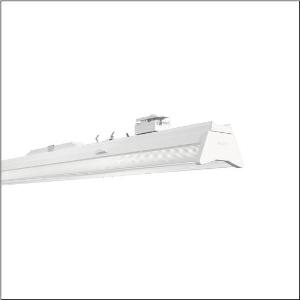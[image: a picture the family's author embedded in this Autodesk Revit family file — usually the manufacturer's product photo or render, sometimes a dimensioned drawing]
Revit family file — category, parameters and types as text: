
# Revit family: licross_21_performance_mo_52td16mn4a5g
name_source: partatom
category: Lighting Fixtures
units: mm (PartAtom-declared; Revit-internal decimal feet)

## family parameters
Cut with Voids When Loaded = No
Host = Face
Light Source = No
Part Type = Normal
Room Calculation Point = No
Round Connector Dimension = Use Diameter
Shared = No

## types (1)
- --- (1 x LED, 10890 lm, 60.5 W, 4000K)
    Apparent Load = 61 VA
    CIE Flux Codes = 66 88 96 79 100
    Color Rendering = 80
    Color Temperature = 4000K
    Default Elevation = 1800 mm
    Description = Licross 21 Performance MO, luminaire insert, of sheet steel, galvanised, coil coated, white, length: 1.500mm, width: 120mm, height: 123mm, LED rated luminous flux: 10.890lm, light colour: 840, SDCM (Standard Deviation of Colour Matching)MacAdam ≤ 3 SDCM (initial), control gear: ON/OFF Multilumen, with plug, 3-pole, with phase selection, mains connection: 220..240V, AC, 50/60Hz, rated input power: 61W, internal wiring halogen-free, primary light control with lens, of plastic, primary optical cover: cover, of PMMA, light emission: direct/indirect distribution, primary light characteristic: symmetric, protection rating (complete): IP54, insulation class (complete): insulation class I (protective earthing), certification: CE, ENEC, UKCA, protection symbol: D if used in an environment with non-conductive dust loads with corresponding accessories, impact resistance: IK06, permissible ambient temperature for indoor applications: -35..+45°C, corresponds to IFS (International Featured Standards) requirements for safety and quality in the food industry, reducing of maximum allowable ambient temperature of 5°C with ceiling mounting, LABS conformity tested according to VDMA 24364:2018-05, The light source and the operating device comply with the requirements of the Ecodesign Regulation (EU) 2019/2020 and are replaceable in accordance with this regulation, packaging unit: 1 piece
    Height = 114 mm
    Lamp = 1 x LED
    Lamp Light Flux = 10890 lm
    Lamp Power = 60.5 W
    Lamp count = 1
    Length = 1500 mm
    Luminous efficacy = 180 lm/W
    Manufacturer = Siteco
    ModVariant = No
    Model = 52TD16MN4A5G
    Mounting Place = Ceiling
    Mounting Type = Pendant
    Number of Poles = 1
    OnlyDefault = Yes
    Power Factor = 1
    Product Name = Licross 21 Performance MO
    Product group = luminaire insert | ceiling pendant
    ProductGroupID = 901
    Protection Class = Protection class I
    Protection Degree = IP 54
    RLX_Detail_Level = 1
    RLX_Emergency_Light_Flux = 0 lm
    RLX_Emergency_Type = 0
    RLX_Emergency_Type_DB = No
    RlxData = <blob elided: 32089 chars, md5=6a0488f3>
    Socket = socket
    Standby Power = 0 W
    System Light Flux = 10890 lm
    System Power = 61 W
    Type Comments = factory setting: luminous flux: 100 % | (A | C | E) | 140 mA
    Type Image = l_1256138.jpg
    URL = http://relux.com
    VarID = @adj_110725
    Voltage = 0 V
    Weight = 0.00 kg
    Width = 120 mm

## geometry (parser evidence)
native form markers: Blend x4, Sweep x11
no freeform markers — native parametric forms only
